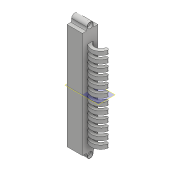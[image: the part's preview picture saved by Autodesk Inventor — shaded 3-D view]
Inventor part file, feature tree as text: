
AUTODESK INVENTOR PART (.ipt)
format: ipt  version: 2017 (Build 210142000, 142)  size: 269,312 bytes
history: native  units: mm
features: extrude x10, sketch x10, move_body x4, plane x2, direct_edit x2, pattern_linear x1, mirror x1, boolean_combine x1
ambient origin geometry x8: Origin, YZ Plane, XZ Plane, XY Plane, X Axis, Y Axis, Z Axis, Center Point
bodies: Solid1 (feature_tree), Solid2 (feature_tree), Solid3 (feature_tree), Solid4 (feature_tree)
feature tree (31):
  extrude  "Extrusion1"  Depth=250.0mm
  plane  "Work Plane1"
  extrude  "Extrusion2"  [1 undecoded]
  pattern_linear  "Rectangular Pattern1"  Count1=14  [1 undecoded]
  extrude  "Extrusion3"  Depth=250.0mm TaperAngle=0.0deg
  plane  "Work Plane2"
  mirror  "Mirror1"
  extrude  "Extrusion4"  Depth=313.75mm TaperAngle=0.0deg
  extrude  "Extrusion5"  Depth=443.75mm TaperAngle=0.0deg
  extrude  "Extrusion6"  TaperAngle=0.0deg  [1 undecoded]
  direct_edit  "Direct Edit1"
  extrude  "Extrusion7"  Depth=1280.5mm TaperAngle=0.0deg
  extrude  "Extrusion8"  Depth=210.0mm TaperAngle=0.0deg
  extrude  "Extrusion9"  TaperAngle=0.0deg  [1 undecoded]
  extrude  "Extrusion10"  [1 undecoded]
  direct_edit  "Direct Edit2"
  boolean_combine  "Combine1"
  sketch  "Sketch1"  dims[d0=250.0mm d1=250.0mm]
  sketch  "Sketch2"  dims[d2=1720.0mm d3=0.0mm d4=-75.0mm]
  sketch  "Sketch3"  dims[d5=60.5mm d6=0.0mm d7=140.0mm d9=120.0mm]
  sketch  "Sketch4"  dims[d10=100.0mm d11=250.0mm d12=0.0mm]
  sketch  "Sketch5"  dims[d13=4000.0mm d14=112.625mm d15=0.0mm d16=0.0mm d17=313.75mm d18=0.0mm]
  sketch  "Sketch6"  dims[d19=2000.0mm d20=443.75mm d21=968.125mm d22=0.0mm d23=0.0mm]
  sketch  "Sketch7"  dims[d24=0.0mm d25=0.0mm d26=-4000.0mm d27=0.0mm d28=0.0mm d29=-4000.0mm]
  sketch  "Sketch8"  dims[d30=1321.0mm d31=0.0mm d32=1280.5mm d33=0.0mm]
  sketch  "Sketch9"  dims[d34=210.0mm d35=0.0mm d36=210.0mm d37=0.0mm]
  sketch  "Sketch10"  dims[d38=0.0mm d39=0.0mm d40=-62.25mm d41=0.0mm d42=0.0mm d43=-75.0mm]
  move_body  "Move1"
  move_body  "Move2"
  move_body  "Move3"
  move_body  "Move4"
note: 5 required parameter values undecoded (feature->parameter linkage not recoverable at this tier; creation-order binding heuristic only, values carry confidence <= 0.55)
